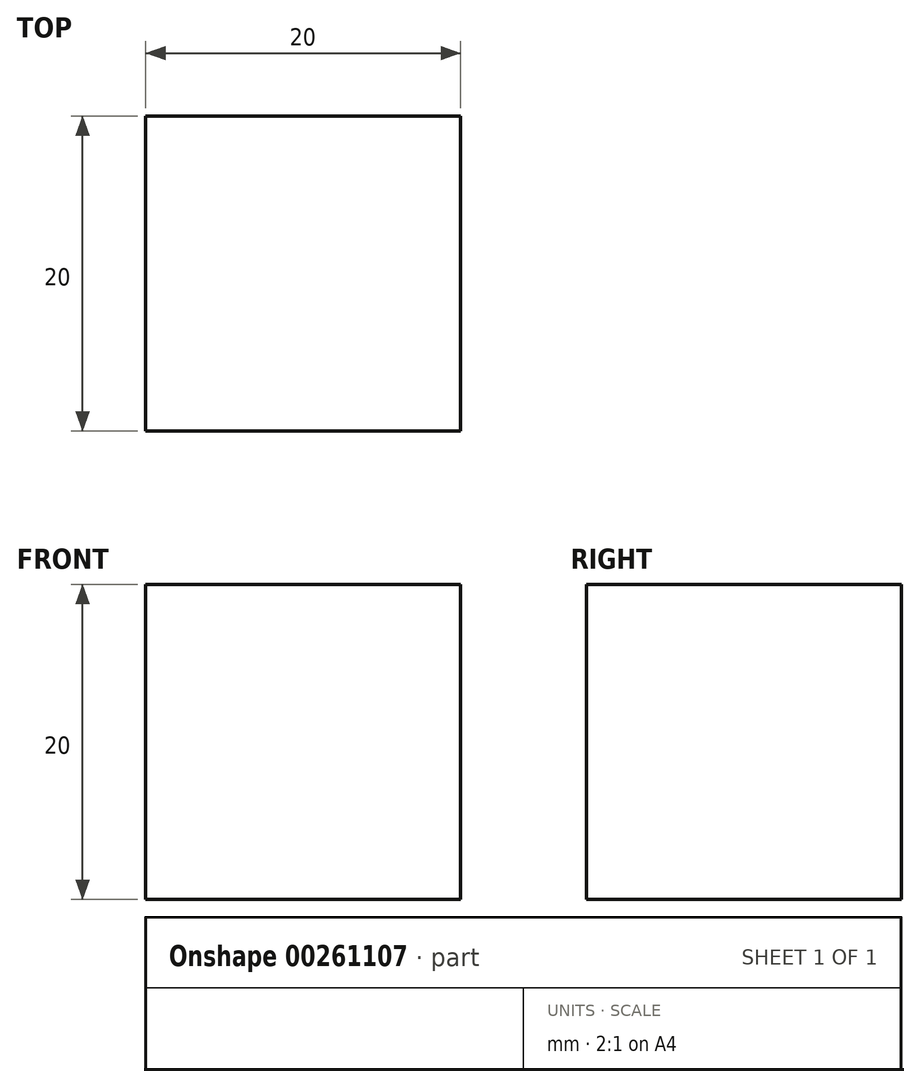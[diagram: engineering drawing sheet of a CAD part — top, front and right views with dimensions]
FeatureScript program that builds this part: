
annotation { "Feature Type Name" : "Feature", "Feature Type Description" : "" }
export const myFeature = defineFeature(function(context is Context, id is Id, definition is map)
    precondition{}
    {
        {
            var Q0;
            Q0=qCreatedBy(makeId("Top.planeOp"),FACE);
            var sketch = newSketch(context, id + "F0", { "sketchPlane" : qUnion([Q0])});
            skLineSegment(sketch, "E0.bottom", {"start": v(-10, 10) * mm, "end": v(10, 10) * mm});
            skLineSegment(sketch, "E0.top", {"start": v(-10, -10) * mm, "end": v(10, -10) * mm});
            skLineSegment(sketch, "E0.left", {"start": v(-10, 10) * mm, "end": v(-10, -10) * mm});
            skLineSegment(sketch, "E0.right", {"start": v(10, 10) * mm, "end": v(10, -10) * mm});
            skPoint(sketch, "E1", {"position": v(0, 10) * mm});
            skPoint(sketch, "E2", {"position": v(10, 0) * mm});
            skSolve(sketch);
        }
        {
            var Q0;
            Q0=makeQuery(id+"F0.imprint","IMPRINT",FACE,{"disambiguationData":[TD([[makeQuery(id+"F0.imprint","IMPRINT",EDGE,{"derivedFrom":sQuery(id+"F0.wireOp",EDGE,"E0.bottom")}),-1.0]])]});
            extrude(context, id + "F1", {"entities" : qUnion([Q0]), "depth" : 20 * mm});
        }
    });
